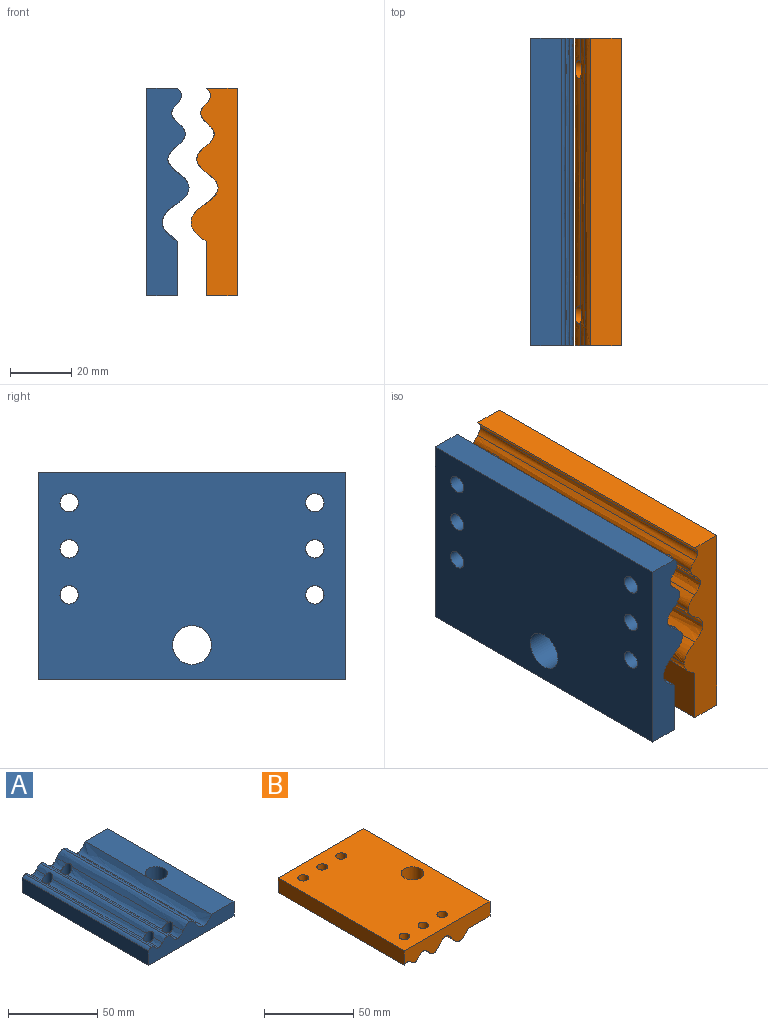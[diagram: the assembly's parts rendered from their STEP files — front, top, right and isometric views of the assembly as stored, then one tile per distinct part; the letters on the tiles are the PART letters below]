
ASSEMBLY  parts=2 mates=1
PART A: 29 faces, bbox 67.7x100x13.8 mm
  f0: extruded ~100x6.25mm, area 758mm2, adj f1,f13,f20,f21,f25,f26
  f1: extruded ~100x5mm, area 645.9mm2, adj f0,f2,f20,f21,f25,f26
  f2: extruded ~100x5mm, area 645.9mm2, adj f1,f3,f4,f5,f20,f21,f22,f27
  f3: extruded ~76.68x4.38mm, area 417.1mm2, adj f2,f6,f22,f27
  f4: extruded ~8.34x4.38mm, area 41.1mm2, adj f2,f6,f20,f27
  f5: extruded ~8.34x4.38mm, area 41.1mm2, adj f2,f6,f21,f22
  f6: extruded ~100x4.38mm, area 550.8mm2, adj f3,f4,f5,f14,f20,f21,f22,f27
  f7: extruded ~100x3.75mm, area 446.8mm2, adj f8,f9,f14,f15,f20,f21,f24,f28
  f8: extruded ~75.32x3.13mm, area 279.6mm2, adj f7,f10,f24,f28
  f9: extruded ~7.66x3.13mm, area 26.9mm2, adj f7,f10,f21,f28
  f10: extruded ~100x3.13mm, area 368.9mm2, adj f8,f9,f15,f16,f20,f21,f24,f28
  f11: plane 100x67.7mm, normal (0,0,-1), area 6473.7mm2, adj f18,f19,f20,f21,f22,f23,f24,f25
  f12: plane 100x17.7mm, normal (0,0,1), area 1643.3mm2, adj f13,f19,f20,f21,f23
  f13: extruded ~100x6.25mm, area 833.6mm2, adj f0,f12,f20,f21
  f14: extruded ~100x3.75mm, area 467mm2, adj f6,f7,f20,f21
  f15: extruded ~7.66x3.13mm, area 26.9mm2, adj f7,f10,f20,f24
  f16: extruded ~100x2.5mm, area 286.9mm2, adj f10,f17,f20,f21
  f17: extruded ~100x2.5mm, area 286.9mm2, adj f16,f18,f20,f21
  f18: plane 100x10mm, normal (-1,0,0), area 1000mm2, adj f11,f17,f20,f21
  f19: plane 100x10mm, normal (1,0,0), area 1000mm2, adj f11,f12,f20,f21
  f20: plane 67.7x13.75mm, normal (0,-1,0), area 651mm2, adj f0,f1,f2,f4,f6,f7,f10,f11
  f21: plane 67.7x13.75mm, normal (0,1,0), area 651mm2, adj f0,f1,f2,f5,f6,f7,f9,f10
  f22: cylinder r=3mm len=10.71mm, axis (0,0,-1), area 154.2mm2, adj f2,f3,f5,f6,f11
  f23: cylinder r=6.35mm len=12.7mm, axis (0,0,-1), area 399mm2, adj f11,f12
  f24: cylinder r=3mm len=11.79mm, axis (0,0,-1), area 179.2mm2, adj f7,f8,f10,f11,f15
  f25: cylinder r=3mm len=10.71mm, axis (0,0,-1), area 138.8mm2, adj f0,f1,f11
  f26: cylinder r=3mm len=10.71mm, axis (0,0,-1), area 138.8mm2, adj f0,f1,f11
  f27: cylinder r=3mm len=10.71mm, axis (0,0,-1), area 154.2mm2, adj f2,f3,f4,f6,f11
  f28: cylinder r=3mm len=11.79mm, axis (0,0,-1), area 179.2mm2, adj f7,f8,f9,f10,f11
PART B: 29 faces, bbox 67.7x100x15 mm
  f0: plane 100x67.7mm, normal (0,0,1), area 6473.7mm2, adj f13,f19,f20,f21,f22,f23,f24,f25
  f1: extruded ~100x3.13mm, area 368.9mm2, adj f2,f3,f4,f15,f20,f21,f27,f28
  f2: extruded ~7.66x3.13mm, area 26.9mm2, adj f1,f5,f20,f28
  f3: extruded ~75.32x3.13mm, area 279.6mm2, adj f1,f5,f27,f28
  f4: extruded ~7.66x3.13mm, area 26.9mm2, adj f1,f5,f21,f27
  f5: extruded ~100x3.75mm, area 446.8mm2, adj f2,f3,f4,f16,f20,f21,f27,f28
  f6: extruded ~100x4.38mm, area 550.8mm2, adj f7,f8,f9,f16,f20,f21,f25,f26
  f7: extruded ~8.34x4.38mm, area 41.1mm2, adj f6,f10,f21,f26
  f8: extruded ~8.34x4.38mm, area 41.1mm2, adj f6,f10,f20,f25
  f9: extruded ~76.68x4.38mm, area 417.1mm2, adj f6,f10,f25,f26
  f10: extruded ~100x5mm, area 645.9mm2, adj f7,f8,f9,f11,f20,f21,f25,f26
  f11: extruded ~100x5mm, area 645.9mm2, adj f10,f12,f20,f21,f23,f24
  f12: extruded ~100x6.25mm, area 757.9mm2, adj f11,f17,f20,f21,f23,f24
  f13: plane 100x10mm, normal (-1,0,0), area 1000mm2, adj f0,f14,f20,f21
  f14: extruded ~100x2.5mm, area 286.9mm2, adj f13,f15,f20,f21
  f15: extruded ~100x2.5mm, area 286.9mm2, adj f1,f14,f20,f21
  f16: extruded ~100x3.75mm, area 467mm2, adj f5,f6,f20,f21
  f17: extruded ~100x6.25mm, area 833.6mm2, adj f12,f18,f20,f21
  f18: plane 100x17.7mm, normal (0,0,-1), area 1643.3mm2, adj f17,f19,f20,f21,f22
  f19: plane 100x10mm, normal (1,0,0), area 1000mm2, adj f0,f18,f20,f21
  f20: plane 67.7x15mm, normal (0,-1,0), area 703mm2, adj f0,f1,f2,f5,f6,f8,f10,f11
  f21: plane 67.7x15mm, normal (0,1,0), area 703mm2, adj f0,f1,f4,f5,f6,f7,f10,f11
  f22: cylinder r=6.35mm len=12.7mm, axis (0,0,1), area 399mm2, adj f0,f18
  f23: cylinder r=3mm len=14.93mm, axis (0,0,1), area 238.2mm2, adj f0,f11,f12
  f24: cylinder r=3mm len=14.93mm, axis (0,0,1), area 238.2mm2, adj f0,f11,f12
  f25: cylinder r=3mm len=13.13mm, axis (0,0,1), area 222.8mm2, adj f0,f6,f8,f9,f10
  f26: cylinder r=3mm len=13.13mm, axis (0,0,1), area 222.8mm2, adj f0,f6,f7,f9,f10
  f27: cylinder r=3mm len=11.88mm, axis (0,0,1), area 197.8mm2, adj f0,f1,f3,f4,f5
  f28: cylinder r=3mm len=11.88mm, axis (0,0,1), area 197.8mm2, adj f0,f1,f2,f3,f5
PLACE A rot(axis=(0,1,0),90deg) t=(76.99,70.48,19.53)mm
PLACE B rot(axis=(0,1,0),90deg) t=(86.44,70.48,19.53)mm
MATE slider B.f22 <-> A.f23  axis (-1,0,0) through (86.44,20.48,-11.82)mm
